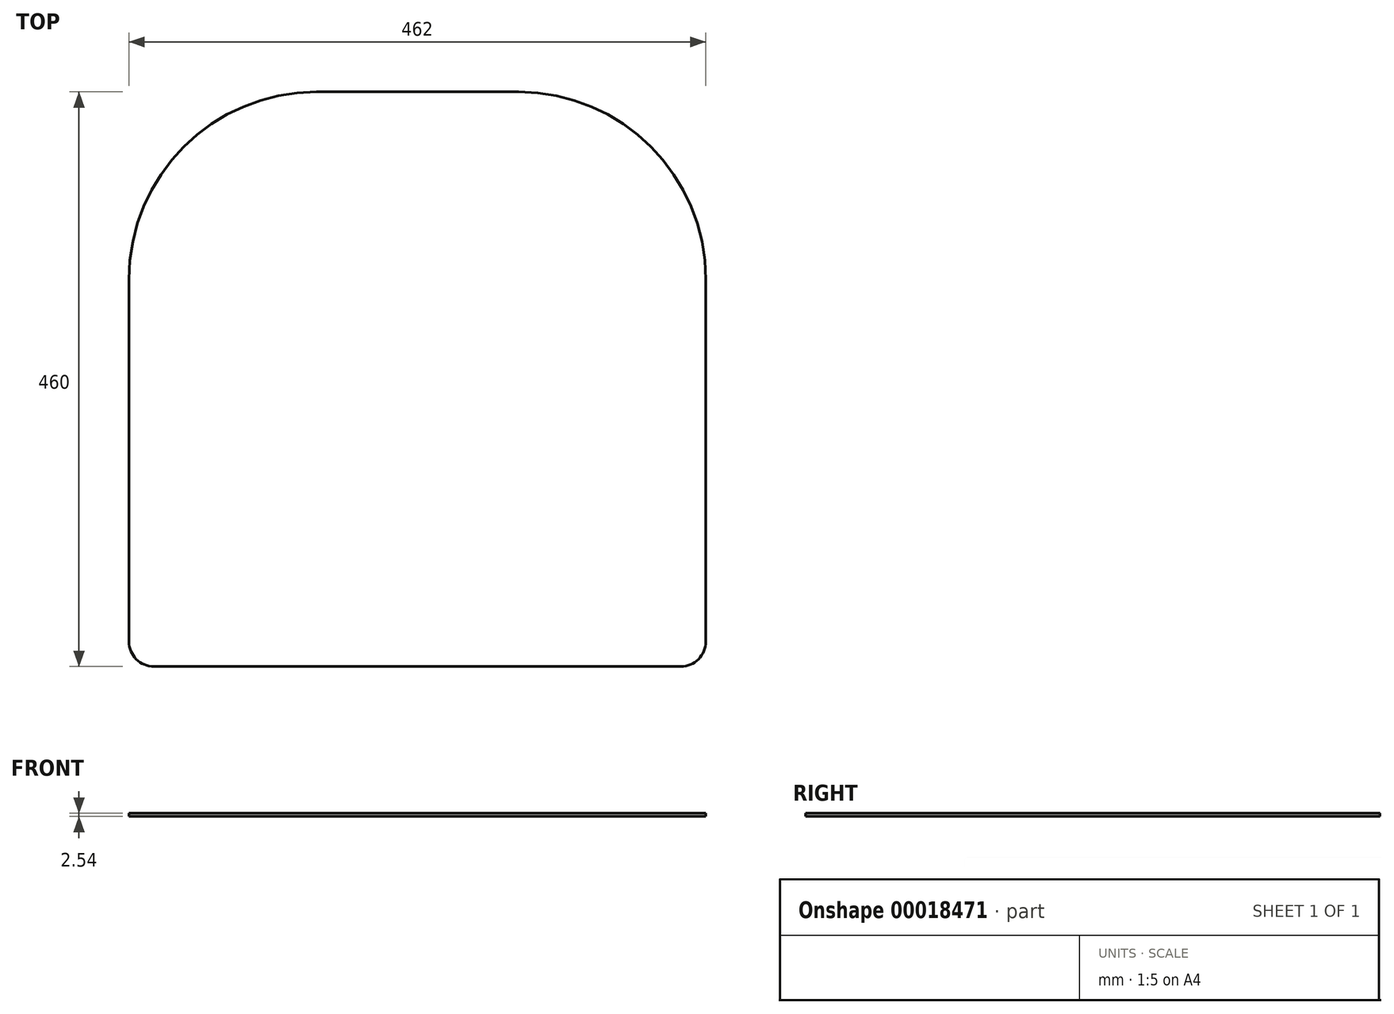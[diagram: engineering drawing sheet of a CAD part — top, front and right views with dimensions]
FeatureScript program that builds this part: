
annotation { "Feature Type Name" : "Feature", "Feature Type Description" : "" }
export const myFeature = defineFeature(function(context is Context, id is Id, definition is map)
    precondition{}
    {
        {
            var Q0;
            Q0=qCreatedBy(makeId("Top.planeOp"),FACE);
            var sketch = newSketch(context, id + "F0", { "sketchPlane" : qUnion([Q0])});
            skLineSegment(sketch, "E0.rect.bottom", {"start": v(211, -230) * mm, "end": v(-211, -230) * mm});
            skLineSegment(sketch, "E0.rect.top", {"start": v(81, 230) * mm, "end": v(-81, 230) * mm});
            skLineSegment(sketch, "E0.rect.left", {"start": v(231, -210) * mm, "end": v(231, 80) * mm});
            skLineSegment(sketch, "E0.rect.right", {"start": v(-231, -210) * mm, "end": v(-231, 80) * mm});
            skPoint(sketch, "E0.rect.middle", {"position": v(0, 0) * mm});
            skPoint(sketch, "E1.visualSharp", {"position": v(-231, -230) * mm});
            skArc(sketch, "E1.filletArc", {"start": v(-231, -210) * mm, "mid": v(-225.14, -224.14) * mm, "end": v(-211, -230) * mm});
            skPoint(sketch, "E2.visualSharp", {"position": v(231, -230) * mm});
            skArc(sketch, "E2.filletArc", {"start": v(211, -230) * mm, "mid": v(225.14, -224.14) * mm, "end": v(231, -210) * mm});
            skPoint(sketch, "E3.visualSharp", {"position": v(-231, 230) * mm});
            skArc(sketch, "E3.filletArc", {"start": v(-81, 230) * mm, "mid": v(-187.07, 186.07) * mm, "end": v(-231, 80) * mm});
            skPoint(sketch, "E4.visualSharp", {"position": v(231, 230) * mm});
            skArc(sketch, "E4.filletArc", {"start": v(231, 80) * mm, "mid": v(187.07, 186.07) * mm, "end": v(81, 230) * mm});
            skSolve(sketch);
        }
        {
            var Q0;
            Q0 = qSketchRegion(id + "F0", true);
            extrude(context, id + "F1", {"entities" : qUnion([Q0]), "depth" : 2.54 * mm});
        }
    });
